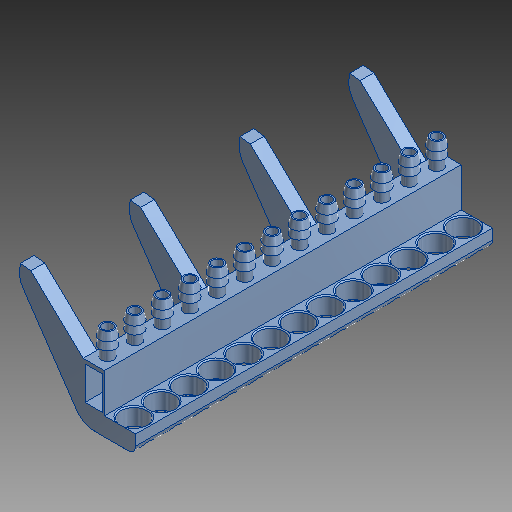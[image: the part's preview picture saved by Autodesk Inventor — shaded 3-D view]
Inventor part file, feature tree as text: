
AUTODESK INVENTOR PART (.ipt)
format: ipt  version: 2018 (Build 220112000, 112)  size: 615,424 bytes
history: native  units: in
note: dims shown in document units (in); Inventor stores cm internally (conversion verified against a paired STEP export)
features: other x11, extrude x7, pattern_linear x4, fillet x3, projected_geometry x1, sketch x1
ambient origin geometry x8: Origin, YZ Plane, XZ Plane, XY Plane, X Axis, Y Axis, Z Axis, Center Point
bodies: Body1 (feature_tree)
feature tree (27):
  other  "CrossSection1"
  other  "Silicone Fitting Plane"
  other  "Cap Plane"
  other  "Base Sketch"
  extrude  "Base"  Depth=0.3214in
  extrude  "Lip"  Depth=0.3214in
  extrude  "Tube Socket"  Depth=0.3214in
  pattern_linear  "Tube Socket Repetition"  Spacing1=0.0197in  [1 undecoded]
  other  "Silicone Fitting"
  pattern_linear  "Silicone Fitting Repetion"  Spacing1=0.5906in  [1 undecoded]
  extrude  "Airflow Cut"  [1 undecoded]
  pattern_linear  "Airflow Cut Repetition"  Spacing1=0.0in  [1 undecoded]
  extrude  "Coupling"  TaperAngle=90.0deg  [1 undecoded]
  extrude  "Cap"  Depth=0.3214in TaperAngle=0.0deg
  extrude  "Arm"  [1 undecoded]
  fillet  "Fillet4"  Radius=5.5118in
  fillet  "Fillet6"  Radius=0.4134in
  other  "Rule Fillet2"
  pattern_linear  "Rectangular Pattern9"  Count1=13  [1 undecoded]
  fillet  "Fillet5"  Radius=0.4134in
  other  "Silicone Fitting Sketch"
  other  "Airflow Cut Sketch"
  projected_geometry  "Projected Loop7"
  other  "Lip Sketch"
  sketch  "Sketch23"  dims[d87=0.0197in d88=0.0787in d89=-1.0625in d90=0.7874in d1=0.0591in d2=0.0591in d3=0.0591in d4=0.0197in d5=0.5906in d6=-0.2067in d8=0.0in d111=90.0deg d112=0.1181in d9=0.0in d12=-5.374in d155=5.5118in d157=0.4134in d158=5.1181in d160=0.4134in d161=5.374in d163=0.3214in d164=0.0in d165=0.4724in d166=0.0in d167=0.3937in d168=0.2067in d169=0.2362in d170=0.3937in d171=0.0in d172=5.1181in d174=0.4134in d188=0.0157in d189=0.3214in d190=0.5906in d200=0.2067in d201=0.0in d202=1.5748in d204=1.6535in d206=0.1181in d207=0.315in d209=0.315in d210=0.0295in d211=0.0295in d212=0.0295in d213=0.0591in d214=0.4134in d215=0.0in d218=0.5906in d219=0.3214in d220=0.0591in d221=0.0in d223=0.0481in]
  other  "Arm Sketch"
  other  "Cap Sketch"
note: 7 required parameter values undecoded (feature->parameter linkage not recoverable at this tier; creation-order binding heuristic only, values carry confidence <= 0.55)
